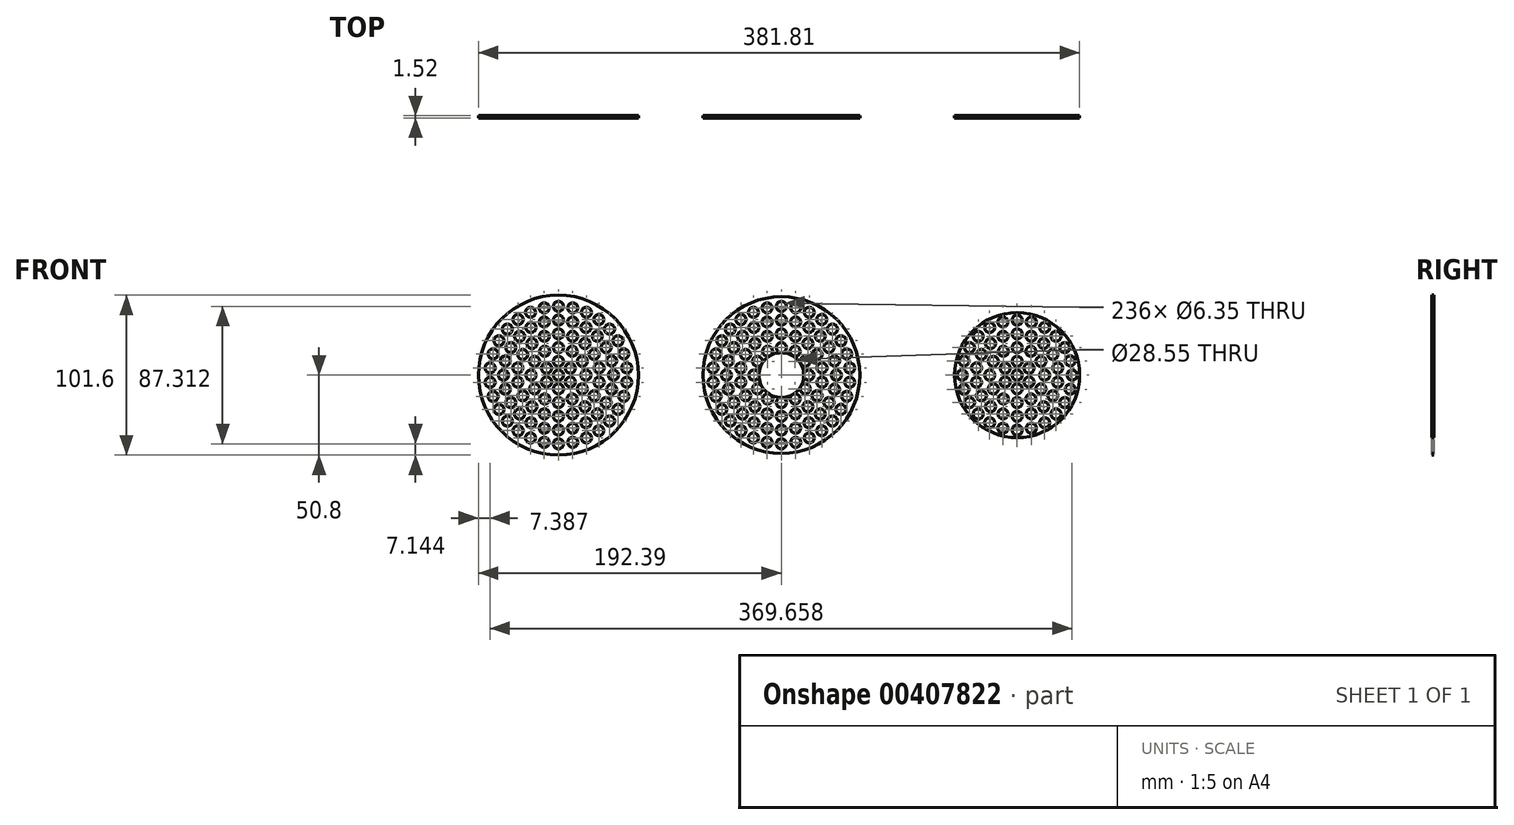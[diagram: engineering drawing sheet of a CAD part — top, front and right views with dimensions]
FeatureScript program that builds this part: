
annotation { "Feature Type Name" : "Feature", "Feature Type Description" : "" }
export const myFeature = defineFeature(function(context is Context, id is Id, definition is map)
    precondition{}
    {
        {
            var Q0;
            Q0=qCreatedBy(makeId("Front.planeOp"),FACE);
            var sketch = newSketch(context, id + "F0", { "sketchPlane" : qUnion([Q0])});
            skCircle(sketch, "E0", {"center": v(0, 0) * mm, "radius": 49.78 * mm});
            skCircle(sketch, "E1", {"center": v(0, 0) * mm, "radius": 14.27 * mm});
            skCircle(sketch, "E2", {"center": v(0, 17.46) * mm, "radius": 3.18 * mm});
            skCircle(sketch, "E3", {"center": v(0, 26.2) * mm, "radius": 3.18 * mm});
            skCircle(sketch, "E4", {"center": v(0, 34.93) * mm, "radius": 3.18 * mm});
            skCircle(sketch, "E5", {"center": v(0, 43.66) * mm, "radius": 3.18 * mm});
            skCircle(sketch, "E6.1.0", {"center": v(-8.73, 15.12) * mm, "radius": 3.18 * mm});
            skCircle(sketch, "E6.2.0", {"center": v(-15.12, 8.73) * mm, "radius": 3.18 * mm});
            skCircle(sketch, "E6.3.0", {"center": v(-17.46, 0) * mm, "radius": 3.18 * mm});
            skCircle(sketch, "E6.4.0", {"center": v(-15.12, -8.73) * mm, "radius": 3.18 * mm});
            skCircle(sketch, "E6.5.0", {"center": v(-8.73, -15.12) * mm, "radius": 3.18 * mm});
            skCircle(sketch, "E6.6.0", {"center": v(0, -17.46) * mm, "radius": 3.18 * mm});
            skCircle(sketch, "E6.7.0", {"center": v(8.73, -15.12) * mm, "radius": 3.18 * mm});
            skCircle(sketch, "E6.8.0", {"center": v(15.12, -8.73) * mm, "radius": 3.18 * mm});
            skCircle(sketch, "E6.9.0", {"center": v(17.46, 0) * mm, "radius": 3.18 * mm});
            skCircle(sketch, "E6.10.0", {"center": v(15.12, 8.73) * mm, "radius": 3.18 * mm});
            skCircle(sketch, "E6.11.0", {"center": v(8.73, 15.12) * mm, "radius": 3.18 * mm});
            skCircle(sketch, "E7.1.0", {"center": v(-8.96, 24.61) * mm, "radius": 3.17 * mm});
            skCircle(sketch, "E7.2.0", {"center": v(-16.84, 20.07) * mm, "radius": 3.18 * mm});
            skCircle(sketch, "E7.3.0", {"center": v(-22.68, 13.1) * mm, "radius": 3.18 * mm});
            skCircle(sketch, "E7.4.0", {"center": v(-25.8, 4.55) * mm, "radius": 3.18 * mm});
            skCircle(sketch, "E7.5.0", {"center": v(-25.8, -4.55) * mm, "radius": 3.18 * mm});
            skCircle(sketch, "E7.6.0", {"center": v(-22.68, -13.1) * mm, "radius": 3.18 * mm});
            skCircle(sketch, "E7.7.0", {"center": v(-16.84, -20.07) * mm, "radius": 3.17 * mm});
            skCircle(sketch, "E7.8.0", {"center": v(-8.96, -24.61) * mm, "radius": 3.18 * mm});
            skCircle(sketch, "E7.9.0", {"center": v(0, -26.2) * mm, "radius": 3.17 * mm});
            skCircle(sketch, "E7.10.0", {"center": v(8.96, -24.61) * mm, "radius": 3.18 * mm});
            skCircle(sketch, "E7.11.0", {"center": v(16.84, -20.07) * mm, "radius": 3.18 * mm});
            skCircle(sketch, "E7.12.0", {"center": v(22.68, -13.1) * mm, "radius": 3.17 * mm});
            skCircle(sketch, "E7.13.0", {"center": v(25.8, -4.55) * mm, "radius": 3.17 * mm});
            skCircle(sketch, "E7.14.0", {"center": v(25.8, 4.55) * mm, "radius": 3.18 * mm});
            skCircle(sketch, "E7.15.0", {"center": v(22.68, 13.1) * mm, "radius": 3.18 * mm});
            skCircle(sketch, "E7.16.0", {"center": v(16.84, 20.07) * mm, "radius": 3.18 * mm});
            skCircle(sketch, "E7.17.0", {"center": v(8.96, 24.61) * mm, "radius": 3.18 * mm});
            skCircle(sketch, "E8.1.0", {"center": v(-9.04, 33.73) * mm, "radius": 3.18 * mm});
            skCircle(sketch, "E8.2.0", {"center": v(-17.46, 30.25) * mm, "radius": 3.18 * mm});
            skCircle(sketch, "E8.3.0", {"center": v(-24.7, 24.7) * mm, "radius": 3.18 * mm});
            skCircle(sketch, "E8.4.0", {"center": v(-30.25, 17.46) * mm, "radius": 3.18 * mm});
            skCircle(sketch, "E8.5.0", {"center": v(-33.73, 9.04) * mm, "radius": 3.18 * mm});
            skCircle(sketch, "E8.6.0", {"center": v(-34.93, 0) * mm, "radius": 3.18 * mm});
            skCircle(sketch, "E8.7.0", {"center": v(-33.73, -9.04) * mm, "radius": 3.18 * mm});
            skCircle(sketch, "E8.8.0", {"center": v(-30.25, -17.46) * mm, "radius": 3.18 * mm});
            skCircle(sketch, "E8.9.0", {"center": v(-24.7, -24.7) * mm, "radius": 3.18 * mm});
            skCircle(sketch, "E8.10.0", {"center": v(-17.46, -30.25) * mm, "radius": 3.18 * mm});
            skCircle(sketch, "E8.11.0", {"center": v(-9.04, -33.73) * mm, "radius": 3.18 * mm});
            skCircle(sketch, "E8.12.0", {"center": v(0, -34.92) * mm, "radius": 3.18 * mm});
            skCircle(sketch, "E8.13.0", {"center": v(9.04, -33.73) * mm, "radius": 3.18 * mm});
            skCircle(sketch, "E8.14.0", {"center": v(17.46, -30.25) * mm, "radius": 3.18 * mm});
            skCircle(sketch, "E8.15.0", {"center": v(24.7, -24.7) * mm, "radius": 3.18 * mm});
            skCircle(sketch, "E8.16.0", {"center": v(30.25, -17.46) * mm, "radius": 3.18 * mm});
            skCircle(sketch, "E8.17.0", {"center": v(33.73, -9.04) * mm, "radius": 3.18 * mm});
            skCircle(sketch, "E8.18.0", {"center": v(34.93, 0) * mm, "radius": 3.18 * mm});
            skCircle(sketch, "E8.19.0", {"center": v(33.73, 9.04) * mm, "radius": 3.18 * mm});
            skCircle(sketch, "E8.20.0", {"center": v(30.25, 17.46) * mm, "radius": 3.18 * mm});
            skCircle(sketch, "E8.21.0", {"center": v(24.7, 24.7) * mm, "radius": 3.18 * mm});
            skCircle(sketch, "E8.22.0", {"center": v(17.46, 30.25) * mm, "radius": 3.18 * mm});
            skCircle(sketch, "E8.23.0", {"center": v(9.04, 33.73) * mm, "radius": 3.18 * mm});
            skCircle(sketch, "E9.1.0", {"center": v(-9.08, 42.7) * mm, "radius": 3.18 * mm});
            skCircle(sketch, "E9.2.0", {"center": v(-17.76, 39.88) * mm, "radius": 3.18 * mm});
            skCircle(sketch, "E9.3.0", {"center": v(-25.66, 35.32) * mm, "radius": 3.18 * mm});
            skCircle(sketch, "E9.4.0", {"center": v(-32.44, 29.21) * mm, "radius": 3.17 * mm});
            skCircle(sketch, "E9.5.0", {"center": v(-37.8, 21.83) * mm, "radius": 3.18 * mm});
            skCircle(sketch, "E9.6.0", {"center": v(-41.52, 13.5) * mm, "radius": 3.18 * mm});
            skCircle(sketch, "E9.7.0", {"center": v(-43.42, 4.56) * mm, "radius": 3.18 * mm});
            skCircle(sketch, "E9.8.0", {"center": v(-43.42, -4.56) * mm, "radius": 3.18 * mm});
            skCircle(sketch, "E9.9.0", {"center": v(-41.52, -13.5) * mm, "radius": 3.18 * mm});
            skCircle(sketch, "E9.10.0", {"center": v(-37.8, -21.83) * mm, "radius": 3.18 * mm});
            skCircle(sketch, "E9.11.0", {"center": v(-32.44, -29.21) * mm, "radius": 3.18 * mm});
            skCircle(sketch, "E9.12.0", {"center": v(-25.66, -35.32) * mm, "radius": 3.18 * mm});
            skCircle(sketch, "E9.13.0", {"center": v(-17.76, -39.88) * mm, "radius": 3.18 * mm});
            skCircle(sketch, "E9.14.0", {"center": v(-9.08, -42.7) * mm, "radius": 3.18 * mm});
            skCircle(sketch, "E9.15.0", {"center": v(0, -43.66) * mm, "radius": 3.18 * mm});
            skCircle(sketch, "E9.16.0", {"center": v(9.08, -42.7) * mm, "radius": 3.18 * mm});
            skCircle(sketch, "E9.17.0", {"center": v(17.76, -39.88) * mm, "radius": 3.17 * mm});
            skCircle(sketch, "E9.18.0", {"center": v(25.66, -35.32) * mm, "radius": 3.18 * mm});
            skCircle(sketch, "E9.19.0", {"center": v(32.44, -29.21) * mm, "radius": 3.18 * mm});
            skCircle(sketch, "E9.20.0", {"center": v(37.8, -21.83) * mm, "radius": 3.18 * mm});
            skCircle(sketch, "E9.21.0", {"center": v(41.52, -13.5) * mm, "radius": 3.18 * mm});
            skCircle(sketch, "E9.22.0", {"center": v(43.42, -4.56) * mm, "radius": 3.18 * mm});
            skCircle(sketch, "E9.23.0", {"center": v(43.42, 4.56) * mm, "radius": 3.18 * mm});
            skCircle(sketch, "E9.24.0", {"center": v(41.52, 13.5) * mm, "radius": 3.18 * mm});
            skCircle(sketch, "E9.25.0", {"center": v(37.8, 21.83) * mm, "radius": 3.18 * mm});
            skCircle(sketch, "E9.26.0", {"center": v(32.44, 29.21) * mm, "radius": 3.18 * mm});
            skCircle(sketch, "E9.27.0", {"center": v(25.66, 35.32) * mm, "radius": 3.18 * mm});
            skCircle(sketch, "E9.28.0", {"center": v(17.76, 39.88) * mm, "radius": 3.18 * mm});
            skCircle(sketch, "E9.29.0", {"center": v(9.08, 42.7) * mm, "radius": 3.18 * mm});
            skCircle(sketch, "E10", {"center": v(-141.59, 0) * mm, "radius": 50.8 * mm});
            skCircle(sketch, "E11", {"center": v(-141.59, 0) * mm, "radius": 3.18 * mm});
            skCircle(sketch, "E12", {"center": v(-141.59, 8.73) * mm, "radius": 3.18 * mm});
            skCircle(sketch, "E13", {"center": v(-141.59, 17.46) * mm, "radius": 3.18 * mm});
            skCircle(sketch, "E14", {"center": v(-141.59, 26.2) * mm, "radius": 3.18 * mm});
            skCircle(sketch, "E15", {"center": v(-141.59, 34.93) * mm, "radius": 3.18 * mm});
            skCircle(sketch, "E16", {"center": v(-141.59, 43.66) * mm, "radius": 3.18 * mm});
            skCircle(sketch, "E17.1.0", {"center": v(-149.15, 4.37) * mm, "radius": 3.18 * mm});
            skCircle(sketch, "E17.2.0", {"center": v(-149.15, -4.37) * mm, "radius": 3.18 * mm});
            skCircle(sketch, "E17.3.0", {"center": v(-141.59, -8.73) * mm, "radius": 3.18 * mm});
            skCircle(sketch, "E17.4.0", {"center": v(-134.02, -4.37) * mm, "radius": 3.18 * mm});
            skCircle(sketch, "E17.5.0", {"center": v(-134.02, 4.37) * mm, "radius": 3.18 * mm});
            skCircle(sketch, "E18.1.0", {"center": v(-150.32, 15.12) * mm, "radius": 3.18 * mm});
            skCircle(sketch, "E18.2.0", {"center": v(-156.7, 8.73) * mm, "radius": 3.18 * mm});
            skCircle(sketch, "E18.3.0", {"center": v(-159.05, 0) * mm, "radius": 3.18 * mm});
            skCircle(sketch, "E18.4.0", {"center": v(-156.7, -8.73) * mm, "radius": 3.18 * mm});
            skCircle(sketch, "E18.5.0", {"center": v(-150.32, -15.12) * mm, "radius": 3.18 * mm});
            skCircle(sketch, "E18.6.0", {"center": v(-141.59, -17.46) * mm, "radius": 3.18 * mm});
            skCircle(sketch, "E18.7.0", {"center": v(-132.86, -15.12) * mm, "radius": 3.18 * mm});
            skCircle(sketch, "E18.8.0", {"center": v(-126.46, -8.73) * mm, "radius": 3.18 * mm});
            skCircle(sketch, "E18.9.0", {"center": v(-124.12, 0) * mm, "radius": 3.18 * mm});
            skCircle(sketch, "E18.10.0", {"center": v(-126.46, 8.73) * mm, "radius": 3.18 * mm});
            skCircle(sketch, "E18.11.0", {"center": v(-132.86, 15.12) * mm, "radius": 3.18 * mm});
            skCircle(sketch, "E19.1.0", {"center": v(-150.55, 24.61) * mm, "radius": 3.17 * mm});
            skCircle(sketch, "E19.2.0", {"center": v(-158.42, 20.07) * mm, "radius": 3.18 * mm});
            skCircle(sketch, "E19.3.0", {"center": v(-164.27, 13.1) * mm, "radius": 3.18 * mm});
            skCircle(sketch, "E19.4.0", {"center": v(-167.38, 4.55) * mm, "radius": 3.18 * mm});
            skCircle(sketch, "E19.5.0", {"center": v(-167.38, -4.55) * mm, "radius": 3.18 * mm});
            skCircle(sketch, "E19.6.0", {"center": v(-164.27, -13.1) * mm, "radius": 3.18 * mm});
            skCircle(sketch, "E19.7.0", {"center": v(-158.42, -20.07) * mm, "radius": 3.17 * mm});
            skCircle(sketch, "E19.8.0", {"center": v(-150.55, -24.61) * mm, "radius": 3.18 * mm});
            skCircle(sketch, "E19.9.0", {"center": v(-141.59, -26.2) * mm, "radius": 3.17 * mm});
            skCircle(sketch, "E19.10.0", {"center": v(-132.63, -24.61) * mm, "radius": 3.18 * mm});
            skCircle(sketch, "E19.11.0", {"center": v(-124.75, -20.07) * mm, "radius": 3.18 * mm});
            skCircle(sketch, "E19.12.0", {"center": v(-118.9, -13.1) * mm, "radius": 3.17 * mm});
            skCircle(sketch, "E19.13.0", {"center": v(-115.8, -4.55) * mm, "radius": 3.17 * mm});
            skCircle(sketch, "E19.14.0", {"center": v(-115.8, 4.55) * mm, "radius": 3.18 * mm});
            skCircle(sketch, "E19.15.0", {"center": v(-118.9, 13.1) * mm, "radius": 3.18 * mm});
            skCircle(sketch, "E19.16.0", {"center": v(-124.75, 20.07) * mm, "radius": 3.18 * mm});
            skCircle(sketch, "E19.17.0", {"center": v(-132.63, 24.61) * mm, "radius": 3.18 * mm});
            skCircle(sketch, "E20.1.0", {"center": v(-150.63, 33.73) * mm, "radius": 3.18 * mm});
            skCircle(sketch, "E20.2.0", {"center": v(-159.05, 30.25) * mm, "radius": 3.18 * mm});
            skCircle(sketch, "E20.3.0", {"center": v(-166.28, 24.7) * mm, "radius": 3.18 * mm});
            skCircle(sketch, "E20.4.0", {"center": v(-171.83, 17.46) * mm, "radius": 3.18 * mm});
            skCircle(sketch, "E20.5.0", {"center": v(-175.32, 9.04) * mm, "radius": 3.18 * mm});
            skCircle(sketch, "E20.6.0", {"center": v(-176.51, 0) * mm, "radius": 3.18 * mm});
            skCircle(sketch, "E20.7.0", {"center": v(-175.32, -9.04) * mm, "radius": 3.18 * mm});
            skCircle(sketch, "E20.8.0", {"center": v(-171.83, -17.46) * mm, "radius": 3.18 * mm});
            skCircle(sketch, "E20.9.0", {"center": v(-166.28, -24.7) * mm, "radius": 3.18 * mm});
            skCircle(sketch, "E20.10.0", {"center": v(-159.05, -30.25) * mm, "radius": 3.18 * mm});
            skCircle(sketch, "E20.11.0", {"center": v(-150.63, -33.73) * mm, "radius": 3.18 * mm});
            skCircle(sketch, "E20.12.0", {"center": v(-141.59, -34.92) * mm, "radius": 3.18 * mm});
            skCircle(sketch, "E20.13.0", {"center": v(-132.55, -33.73) * mm, "radius": 3.18 * mm});
            skCircle(sketch, "E20.14.0", {"center": v(-124.12, -30.25) * mm, "radius": 3.18 * mm});
            skCircle(sketch, "E20.15.0", {"center": v(-116.9, -24.7) * mm, "radius": 3.18 * mm});
            skCircle(sketch, "E20.16.0", {"center": v(-111.34, -17.46) * mm, "radius": 3.18 * mm});
            skCircle(sketch, "E20.17.0", {"center": v(-107.85, -9.04) * mm, "radius": 3.18 * mm});
            skCircle(sketch, "E20.18.0", {"center": v(-106.66, 0) * mm, "radius": 3.18 * mm});
            skCircle(sketch, "E20.19.0", {"center": v(-107.85, 9.04) * mm, "radius": 3.18 * mm});
            skCircle(sketch, "E20.20.0", {"center": v(-111.34, 17.46) * mm, "radius": 3.18 * mm});
            skCircle(sketch, "E20.21.0", {"center": v(-116.9, 24.7) * mm, "radius": 3.18 * mm});
            skCircle(sketch, "E20.22.0", {"center": v(-124.12, 30.25) * mm, "radius": 3.18 * mm});
            skCircle(sketch, "E20.23.0", {"center": v(-132.55, 33.73) * mm, "radius": 3.18 * mm});
            skCircle(sketch, "E21.1.0", {"center": v(-150.66, 42.7) * mm, "radius": 3.18 * mm});
            skCircle(sketch, "E21.2.0", {"center": v(-159.34, 39.88) * mm, "radius": 3.18 * mm});
            skCircle(sketch, "E21.3.0", {"center": v(-167.25, 35.32) * mm, "radius": 3.18 * mm});
            skCircle(sketch, "E21.4.0", {"center": v(-174.03, 29.21) * mm, "radius": 3.17 * mm});
            skCircle(sketch, "E21.5.0", {"center": v(-179.4, 21.83) * mm, "radius": 3.18 * mm});
            skCircle(sketch, "E21.6.0", {"center": v(-183.1, 13.5) * mm, "radius": 3.18 * mm});
            skCircle(sketch, "E21.7.0", {"center": v(-185, 4.56) * mm, "radius": 3.18 * mm});
            skCircle(sketch, "E21.8.0", {"center": v(-185, -4.56) * mm, "radius": 3.18 * mm});
            skCircle(sketch, "E21.9.0", {"center": v(-183.1, -13.5) * mm, "radius": 3.18 * mm});
            skCircle(sketch, "E21.10.0", {"center": v(-179.4, -21.83) * mm, "radius": 3.18 * mm});
            skCircle(sketch, "E21.11.0", {"center": v(-174.03, -29.21) * mm, "radius": 3.18 * mm});
            skCircle(sketch, "E21.12.0", {"center": v(-167.25, -35.32) * mm, "radius": 3.18 * mm});
            skCircle(sketch, "E21.13.0", {"center": v(-159.34, -39.88) * mm, "radius": 3.18 * mm});
            skCircle(sketch, "E21.14.0", {"center": v(-150.66, -42.7) * mm, "radius": 3.18 * mm});
            skCircle(sketch, "E21.15.0", {"center": v(-141.59, -43.66) * mm, "radius": 3.18 * mm});
            skCircle(sketch, "E21.16.0", {"center": v(-132.5, -42.7) * mm, "radius": 3.18 * mm});
            skCircle(sketch, "E21.17.0", {"center": v(-123.83, -39.88) * mm, "radius": 3.17 * mm});
            skCircle(sketch, "E21.18.0", {"center": v(-115.93, -35.32) * mm, "radius": 3.18 * mm});
            skCircle(sketch, "E21.19.0", {"center": v(-109.14, -29.21) * mm, "radius": 3.18 * mm});
            skCircle(sketch, "E21.20.0", {"center": v(-103.78, -21.83) * mm, "radius": 3.18 * mm});
            skCircle(sketch, "E21.21.0", {"center": v(-100.07, -13.5) * mm, "radius": 3.18 * mm});
            skCircle(sketch, "E21.22.0", {"center": v(-98.17, -4.56) * mm, "radius": 3.18 * mm});
            skCircle(sketch, "E21.23.0", {"center": v(-98.17, 4.56) * mm, "radius": 3.18 * mm});
            skCircle(sketch, "E21.24.0", {"center": v(-100.07, 13.5) * mm, "radius": 3.18 * mm});
            skCircle(sketch, "E21.25.0", {"center": v(-103.78, 21.83) * mm, "radius": 3.18 * mm});
            skCircle(sketch, "E21.26.0", {"center": v(-109.14, 29.21) * mm, "radius": 3.18 * mm});
            skCircle(sketch, "E21.27.0", {"center": v(-115.93, 35.32) * mm, "radius": 3.18 * mm});
            skCircle(sketch, "E21.28.0", {"center": v(-123.83, 39.88) * mm, "radius": 3.18 * mm});
            skCircle(sketch, "E21.29.0", {"center": v(-132.5, 42.7) * mm, "radius": 3.18 * mm});
            skCircle(sketch, "E22", {"center": v(149.73, 0) * mm, "radius": 39.69 * mm});
            skCircle(sketch, "E23", {"center": v(149.73, 0) * mm, "radius": 3.18 * mm});
            skCircle(sketch, "E24", {"center": v(149.73, 8.73) * mm, "radius": 3.18 * mm});
            skCircle(sketch, "E25", {"center": v(149.73, 17.46) * mm, "radius": 3.18 * mm});
            skCircle(sketch, "E26", {"center": v(149.73, 26.2) * mm, "radius": 3.18 * mm});
            skCircle(sketch, "E27", {"center": v(149.73, 34.93) * mm, "radius": 3.18 * mm});
            skCircle(sketch, "E28.1.0", {"center": v(142.17, 4.37) * mm, "radius": 3.18 * mm});
            skCircle(sketch, "E28.2.0", {"center": v(142.17, -4.37) * mm, "radius": 3.18 * mm});
            skCircle(sketch, "E28.3.0", {"center": v(149.73, -8.73) * mm, "radius": 3.18 * mm});
            skCircle(sketch, "E28.4.0", {"center": v(157.3, -4.37) * mm, "radius": 3.18 * mm});
            skCircle(sketch, "E28.5.0", {"center": v(157.3, 4.37) * mm, "radius": 3.18 * mm});
            skCircle(sketch, "E29.1.0", {"center": v(141, 15.12) * mm, "radius": 3.18 * mm});
            skCircle(sketch, "E29.2.0", {"center": v(134.6, 8.73) * mm, "radius": 3.18 * mm});
            skCircle(sketch, "E29.3.0", {"center": v(132.27, 0) * mm, "radius": 3.18 * mm});
            skCircle(sketch, "E29.4.0", {"center": v(134.6, -8.73) * mm, "radius": 3.18 * mm});
            skCircle(sketch, "E29.5.0", {"center": v(141, -15.12) * mm, "radius": 3.18 * mm});
            skCircle(sketch, "E29.6.0", {"center": v(149.73, -17.46) * mm, "radius": 3.18 * mm});
            skCircle(sketch, "E29.7.0", {"center": v(158.46, -15.12) * mm, "radius": 3.18 * mm});
            skCircle(sketch, "E29.8.0", {"center": v(164.85, -8.73) * mm, "radius": 3.18 * mm});
            skCircle(sketch, "E29.9.0", {"center": v(167.2, 0) * mm, "radius": 3.18 * mm});
            skCircle(sketch, "E29.10.0", {"center": v(164.85, 8.73) * mm, "radius": 3.18 * mm});
            skCircle(sketch, "E29.11.0", {"center": v(158.46, 15.12) * mm, "radius": 3.18 * mm});
            skCircle(sketch, "E30.1.0", {"center": v(140.77, 24.61) * mm, "radius": 3.17 * mm});
            skCircle(sketch, "E30.2.0", {"center": v(132.9, 20.07) * mm, "radius": 3.18 * mm});
            skCircle(sketch, "E30.3.0", {"center": v(127.05, 13.1) * mm, "radius": 3.18 * mm});
            skCircle(sketch, "E30.4.0", {"center": v(123.93, 4.55) * mm, "radius": 3.18 * mm});
            skCircle(sketch, "E30.5.0", {"center": v(123.93, -4.55) * mm, "radius": 3.18 * mm});
            skCircle(sketch, "E30.6.0", {"center": v(127.05, -13.1) * mm, "radius": 3.18 * mm});
            skCircle(sketch, "E30.7.0", {"center": v(132.9, -20.07) * mm, "radius": 3.17 * mm});
            skCircle(sketch, "E30.8.0", {"center": v(140.77, -24.61) * mm, "radius": 3.18 * mm});
            skCircle(sketch, "E30.9.0", {"center": v(149.73, -26.2) * mm, "radius": 3.17 * mm});
            skCircle(sketch, "E30.10.0", {"center": v(158.69, -24.61) * mm, "radius": 3.18 * mm});
            skCircle(sketch, "E30.11.0", {"center": v(166.57, -20.07) * mm, "radius": 3.18 * mm});
            skCircle(sketch, "E30.12.0", {"center": v(172.41, -13.1) * mm, "radius": 3.17 * mm});
            skCircle(sketch, "E30.13.0", {"center": v(175.53, -4.55) * mm, "radius": 3.17 * mm});
            skCircle(sketch, "E30.14.0", {"center": v(175.53, 4.55) * mm, "radius": 3.18 * mm});
            skCircle(sketch, "E30.15.0", {"center": v(172.41, 13.1) * mm, "radius": 3.18 * mm});
            skCircle(sketch, "E30.16.0", {"center": v(166.57, 20.07) * mm, "radius": 3.18 * mm});
            skCircle(sketch, "E30.17.0", {"center": v(158.69, 24.61) * mm, "radius": 3.18 * mm});
            skCircle(sketch, "E31.1.0", {"center": v(140.7, 33.73) * mm, "radius": 3.18 * mm});
            skCircle(sketch, "E31.2.0", {"center": v(132.27, 30.25) * mm, "radius": 3.18 * mm});
            skCircle(sketch, "E31.3.0", {"center": v(125.03, 24.7) * mm, "radius": 3.18 * mm});
            skCircle(sketch, "E31.4.0", {"center": v(119.48, 17.46) * mm, "radius": 3.18 * mm});
            skCircle(sketch, "E31.5.0", {"center": v(116, 9.04) * mm, "radius": 3.18 * mm});
            skCircle(sketch, "E31.6.0", {"center": v(114.8, 0) * mm, "radius": 3.18 * mm});
            skCircle(sketch, "E31.7.0", {"center": v(116, -9.04) * mm, "radius": 3.18 * mm});
            skCircle(sketch, "E31.8.0", {"center": v(119.48, -17.46) * mm, "radius": 3.18 * mm});
            skCircle(sketch, "E31.9.0", {"center": v(125.03, -24.7) * mm, "radius": 3.18 * mm});
            skCircle(sketch, "E31.10.0", {"center": v(132.27, -30.25) * mm, "radius": 3.18 * mm});
            skCircle(sketch, "E31.11.0", {"center": v(140.7, -33.73) * mm, "radius": 3.18 * mm});
            skCircle(sketch, "E31.12.0", {"center": v(149.73, -34.92) * mm, "radius": 3.18 * mm});
            skCircle(sketch, "E31.13.0", {"center": v(158.77, -33.73) * mm, "radius": 3.18 * mm});
            skCircle(sketch, "E31.14.0", {"center": v(167.2, -30.25) * mm, "radius": 3.18 * mm});
            skCircle(sketch, "E31.15.0", {"center": v(174.43, -24.7) * mm, "radius": 3.18 * mm});
            skCircle(sketch, "E31.16.0", {"center": v(179.98, -17.46) * mm, "radius": 3.18 * mm});
            skCircle(sketch, "E31.17.0", {"center": v(183.46, -9.04) * mm, "radius": 3.18 * mm});
            skCircle(sketch, "E31.18.0", {"center": v(184.65, 0) * mm, "radius": 3.18 * mm});
            skCircle(sketch, "E31.19.0", {"center": v(183.46, 9.04) * mm, "radius": 3.18 * mm});
            skCircle(sketch, "E31.20.0", {"center": v(179.98, 17.46) * mm, "radius": 3.18 * mm});
            skCircle(sketch, "E31.21.0", {"center": v(174.43, 24.7) * mm, "radius": 3.18 * mm});
            skCircle(sketch, "E31.22.0", {"center": v(167.2, 30.25) * mm, "radius": 3.18 * mm});
            skCircle(sketch, "E31.23.0", {"center": v(158.77, 33.73) * mm, "radius": 3.18 * mm});
            skSolve(sketch);
        }
        {
            var Q0;
            Q0=makeQuery(id+"F0.imprint","IMPRINT",FACE,{"disambiguationData":[TD([[makeQuery(id+"F0.imprint","IMPRINT",EDGE,{"derivedFrom":sQuery(id+"F0.wireOp",EDGE,"E10")}),1.0]])]});
            var Q1;
            Q1=makeQuery(id+"F0.imprint","IMPRINT",FACE,{"disambiguationData":[TD([[makeQuery(id+"F0.imprint","IMPRINT",EDGE,{"derivedFrom":sQuery(id+"F0.wireOp",EDGE,"E0")}),1.0]])]});
            var Q2;
            Q2=makeQuery(id+"F0.imprint","IMPRINT",FACE,{"disambiguationData":[TD([[makeQuery(id+"F0.imprint","IMPRINT",EDGE,{"derivedFrom":sQuery(id+"F0.wireOp",EDGE,"E22")}),1.0]])]});
            extrude(context, id + "F1", {"entities" : qUnion([Q0, Q1, Q2]), "depth" : 1.52 * mm});
        }
    });
